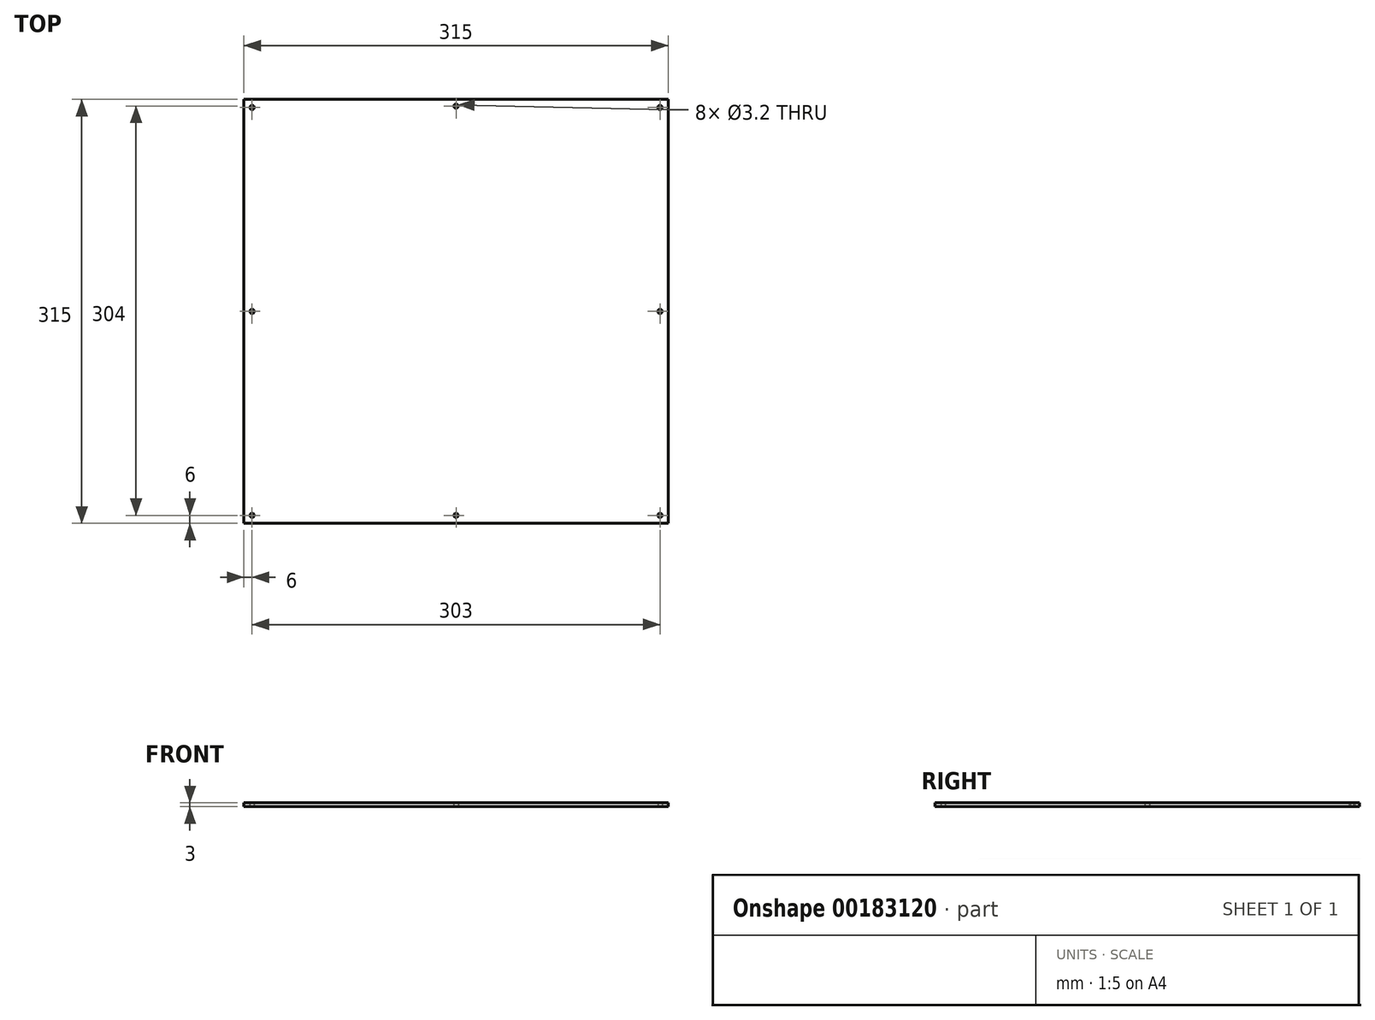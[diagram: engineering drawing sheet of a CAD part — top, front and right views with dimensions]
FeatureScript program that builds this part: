
annotation { "Feature Type Name" : "Feature", "Feature Type Description" : "" }
export const myFeature = defineFeature(function(context is Context, id is Id, definition is map)
    precondition{}
    {
        {
            var Q0;
            Q0=qCreatedBy(makeId("Top.planeOp"),FACE);
            var sketch = newSketch(context, id + "F0", { "sketchPlane" : qUnion([Q0])});
            skLineSegment(sketch, "E0.left", {"start": v(-157.5, 157.5) * mm, "end": v(-157.5, -157.5) * mm});
            skLineSegment(sketch, "E0.right", {"start": v(157.5, 157.5) * mm, "end": v(157.5, -157.5) * mm});
            skPoint(sketch, "E0.middle", {"position": v(0, 0) * mm});
            skLineSegment(sketch, "E1", {"start": v(0, 158.5) * mm, "end": v(0, 152.5) * mm});
            skPoint(sketch, "E1.endSnap0", {"position": v(0, 157.5) * mm});
            skLineSegment(sketch, "E2", {"start": v(-157.5, 0) * mm, "end": v(-151.5, 0) * mm});
            skLineSegment(sketch, "E3", {"start": v(157.5, 0) * mm, "end": v(151.5, 0) * mm});
            skLineSegment(sketch, "E4", {"start": v(0, -157.5) * mm, "end": v(0, -151.5) * mm});
            skPoint(sketch, "E4.endSnap0", {"position": v(0, -156.5) * mm});
            skCircle(sketch, "E5", {"center": v(0, 152.5) * mm, "radius": 1.6 * mm});
            skCircle(sketch, "E6", {"center": v(-151.5, 0) * mm, "radius": 1.6 * mm});
            skCircle(sketch, "E7", {"center": v(151.5, 0) * mm, "radius": 1.6 * mm});
            skCircle(sketch, "E8", {"center": v(0, -151.5) * mm, "radius": 1.6 * mm});
            skPoint(sketch, "E9.startSnap0", {"position": v(154.5, 0) * mm});
            skLineSegment(sketch, "E10", {"start": v(-157.5, 157.5) * mm, "end": v(-151.5, 157.5) * mm});
            skLineSegment(sketch, "E11", {"start": v(-151.5, 157.5) * mm, "end": v(-151.5, 151.5) * mm});
            skLineSegment(sketch, "E12", {"start": v(157.5, 157.5) * mm, "end": v(151.5, 157.5) * mm});
            skLineSegment(sketch, "E13", {"start": v(151.5, 157.5) * mm, "end": v(151.5, 151.5) * mm});
            skLineSegment(sketch, "E14", {"start": v(157.5, -157.5) * mm, "end": v(151.5, -157.5) * mm});
            skLineSegment(sketch, "E15", {"start": v(151.5, -157.5) * mm, "end": v(151.5, -151.5) * mm});
            skLineSegment(sketch, "E16", {"start": v(-157.5, -157.5) * mm, "end": v(-151.5, -157.5) * mm});
            skLineSegment(sketch, "E17", {"start": v(-151.5, -157.5) * mm, "end": v(-151.5, -151.5) * mm});
            skCircle(sketch, "E18", {"center": v(-151.5, 151.5) * mm, "radius": 1.6 * mm});
            skCircle(sketch, "E19", {"center": v(151.5, 151.5) * mm, "radius": 1.6 * mm});
            skCircle(sketch, "E20", {"center": v(151.5, -151.5) * mm, "radius": 1.6 * mm});
            skCircle(sketch, "E21", {"center": v(-151.5, -151.5) * mm, "radius": 1.6 * mm});
            skLineSegment(sketch, "E22", {"start": v(-157.5, 157.5) * mm, "end": v(157.5, 157.5) * mm});
            skLineSegment(sketch, "E23", {"start": v(-157.5, -157.5) * mm, "end": v(157.5, -157.5) * mm});
            skSolve(sketch);
        }
        {
            var Q0;
            Q0=makeQuery(id+"F0.imprint","IMPRINT",FACE,{"disambiguationData":[TD([[makeQuery(id+"F0.imprint","IMPRINT",EDGE,{"derivedFrom":sQuery(id+"F0.wireOp",EDGE,"E5")}),-1.0]])]});
            extrude(context, id + "F1", {"entities" : qUnion([Q0]), "depth" : 3 * mm});
        }
    });
